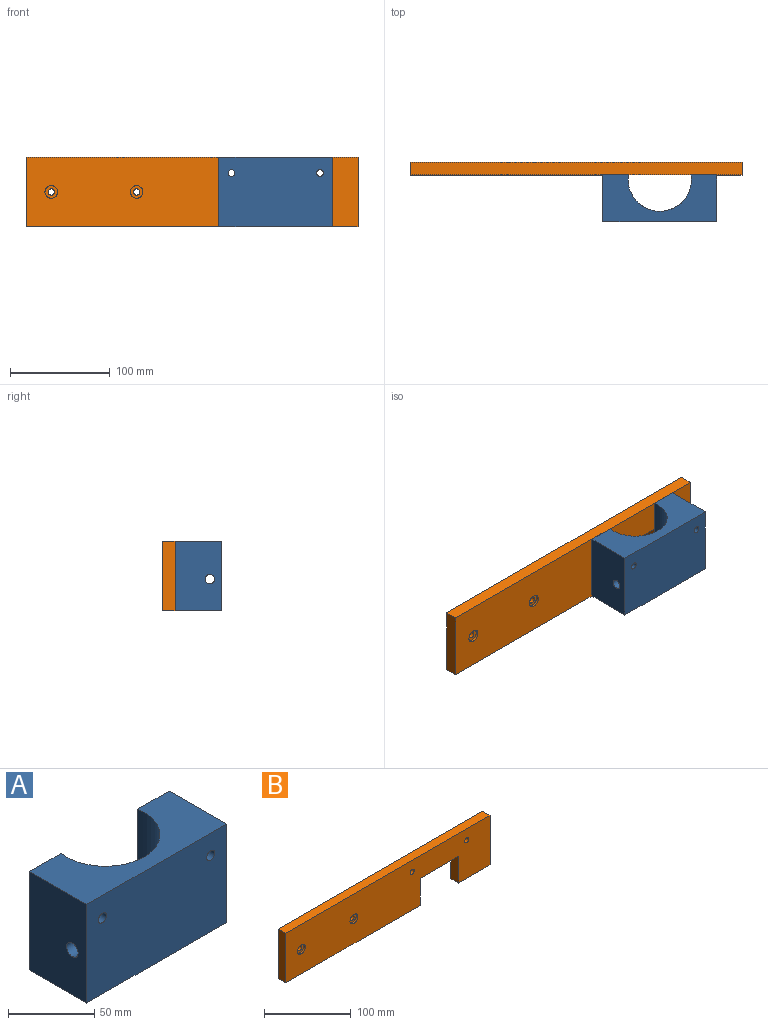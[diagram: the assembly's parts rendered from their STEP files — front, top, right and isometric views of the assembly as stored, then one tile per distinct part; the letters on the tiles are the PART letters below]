
ASSEMBLY  parts=2 mates=1
PART A: 13 faces, bbox 114.3x46.8x69.9 mm
  f0: cylinder r=31.75mm len=69.85mm, axis (0,0,-1), area 7062.4mm2, adj f1,f2,f6,f7,f8,f9,f10
  f1: cylinder r=4.76mm len=50.8mm, axis (1,0,0), area 1369mm2, adj f0,f3,f9
  f2: plane 114.3x46.83mm, normal (0,0,1), area 3468.1mm2, adj f0,f3,f4,f5,f7,f8
  f3: plane 69.85x46.83mm, normal (-1,0,0), area 3199.9mm2, adj f1,f2,f4,f6,f8
  f4: plane 114.3x69.85mm, normal (0,-1,0), area 7912.1mm2, adj f2,f3,f5,f6,f11,f12
  f5: plane 69.85x46.83mm, normal (1,0,0), area 3073.2mm2, adj f2,f4,f6,f7,f10
  f6: plane 114.3x46.83mm, normal (0,0,-1), area 3468.1mm2, adj f0,f3,f4,f5,f7,f8
  f7: plane 69.85x25.76mm, normal (0,1,0), area 1763.4mm2, adj f0,f2,f5,f6,f12
  f8: plane 69.85x25.76mm, normal (0,1,0), area 1763.4mm2, adj f0,f2,f3,f6,f11
  f9: plane 15.76x6.99mm, normal (1,0,0), area 57.3mm2, adj f0,f1,f10
  f10: cylinder r=7.94mm len=63.5mm, axis (1,0,0), area 2497.5mm2, adj f0,f5,f9
  f11: cylinder r=3.38mm len=46.83mm, axis (0,-1,0), area 994mm2, adj f4,f8
  f12: cylinder r=3.38mm len=46.83mm, axis (0,-1,0), area 994mm2, adj f4,f7
PART B: 18 faces, bbox 333.4x12.7x69.9 mm
  f0: plane 51.16x12.7mm, normal (0,0,-1), area 649.7mm2, adj f1,f3,f4,f8
  f1: plane 333.38x69.85mm, normal (0,1,0), area 20759.2mm2, adj f0,f2,f4,f5,f6,f7,f8,f9
  f2: plane 69.85x12.7mm, normal (-1,0,0), area 887.1mm2, adj f1,f3,f5,f6
  f3: plane 333.38x69.85mm, normal (0,-1,0), area 20569.2mm2, adj f0,f2,f4,f5,f6,f7,f8,f9
  f4: plane 69.85x12.7mm, normal (1,0,0), area 887.1mm2, adj f0,f1,f3,f5
  f5: plane 333.38x12.7mm, normal (0,0,1), area 4233.9mm2, adj f1,f2,f3,f4
  f6: plane 219.43x12.7mm, normal (0,0,-1), area 2786.8mm2, adj f1,f2,f3,f7
  f7: plane 38.1x12.7mm, normal (1,0,0), area 483.9mm2, adj f1,f3,f6,f9
  f8: plane 38.1x12.7mm, normal (-1,0,0), area 483.9mm2, adj f0,f1,f3,f9
  f9: plane 62.78x12.7mm, normal (0,0,-1), area 797.3mm2, adj f1,f3,f7,f8
  f10: cylinder r=3.17mm len=10.16mm, axis (0,-1,0), area 202.7mm2, adj f1,f11
  f11: plane 12.7x12.7mm, normal (0,-1,0), area 95mm2, adj f10,f12
  f12: cylinder r=6.35mm len=12.7mm, axis (0,-1,0), area 101.3mm2, adj f3,f11
  f13: cylinder r=3.17mm len=10.16mm, axis (0,-1,0), area 202.7mm2, adj f1,f14
  f14: plane 12.7x12.7mm, normal (0,-1,0), area 95mm2, adj f13,f15
  f15: cylinder r=6.35mm len=12.7mm, axis (0,-1,0), area 101.3mm2, adj f3,f14
  f16: cylinder r=3.38mm len=12.7mm, axis (0,-1,0), area 269.6mm2, adj f1,f3
  f17: cylinder r=3.38mm len=12.7mm, axis (0,-1,0), area 269.6mm2, adj f1,f3
PLACE A at identity
PLACE B at identity fixed
MATE fastened B.f6 <-> A.f6  axis (0,0,-1) through (-31.39,4.76,38.1)mm
